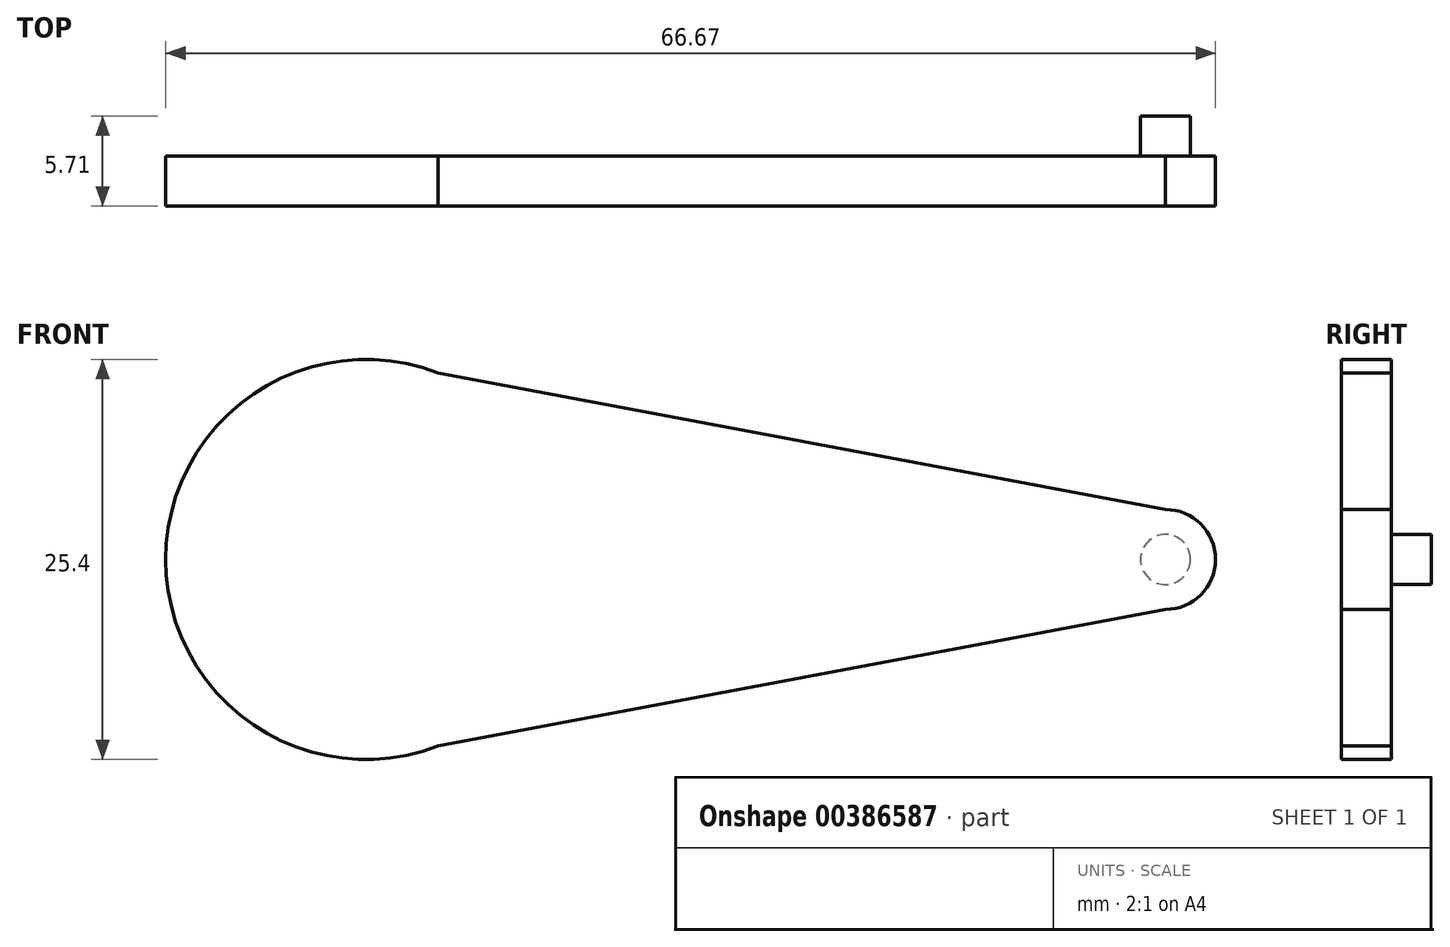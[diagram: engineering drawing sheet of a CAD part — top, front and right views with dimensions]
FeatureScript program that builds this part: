
annotation { "Feature Type Name" : "Feature", "Feature Type Description" : "" }
export const myFeature = defineFeature(function(context is Context, id is Id, definition is map)
    precondition{}
    {
        {
            var Q0;
            Q0=qCreatedBy(makeId("Front.planeOp"),FACE);
            var sketch = newSketch(context, id + "F0", { "sketchPlane" : qUnion([Q0])});
            skArc(sketch, "E0", {"start": v(4.6, 11.84) * mm, "mid": v(-12.7, 0) * mm, "end": v(4.6, -11.84) * mm});
            skArc(sketch, "E1", {"start": v(50.8, -3.18) * mm, "mid": v(53.98, 0) * mm, "end": v(50.8, 3.17) * mm});
            skLineSegment(sketch, "E2", {"start": v(0, 12.7) * mm, "end": v(50.8, 3.17) * mm});
            skLineSegment(sketch, "E3", {"start": v(0, -12.7) * mm, "end": v(50.8, -3.18) * mm});
            skSolve(sketch);
        }
        {
            var Q0;
            Q0 = qSketchRegion(id + "F0", true);
            extrude(context, id + "F1", {"entities" : qUnion([Q0]), "depth" : 3.17 * mm});
        }
        {
            var Q0;
            Q0=makeQuery(id+"F1.opExtrude","CAP_FACE",FACE,{"disambiguationData":[OSD([sQuery(id+"F0.wireOp",EDGE,"E0"),sQuery(id+"F0.wireOp",EDGE,"E1"),sQuery(id+"F0.wireOp",EDGE,"E2"),sQuery(id+"F0.wireOp",EDGE,"E3")])],"isStart":true});
            var sketch = newSketch(context, id + "F2", { "sketchPlane" : qUnion([Q0])});
            skCircle(sketch, "E4", {"center": v(-50.8, 0) * mm, "radius": 1.59 * mm});
            skSolve(sketch);
        }
        {
            var Q0;
            Q0 = qSketchRegion(id + "F2", true);
            extrude(context, id + "F3", {"entities" : qUnion([Q0]), "operationType" : NewBodyOperationType.ADD, "depth" : 2.54 * mm});
        }
    });
